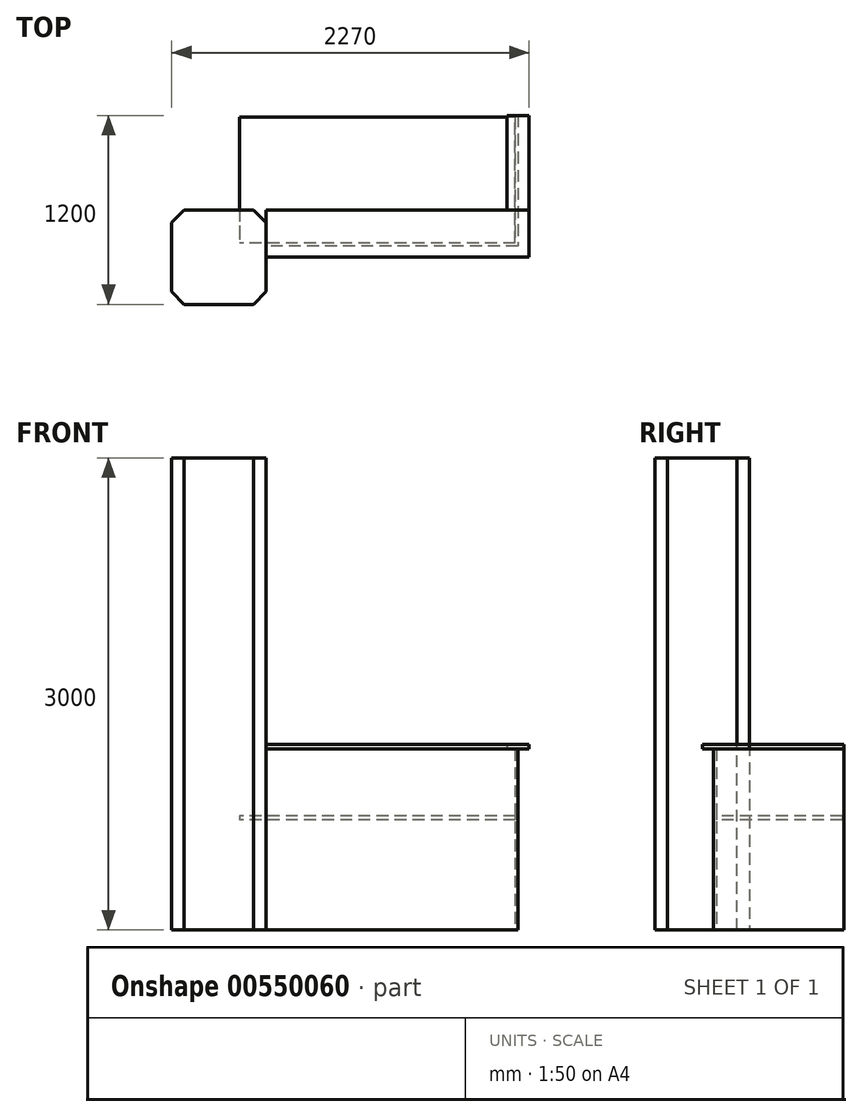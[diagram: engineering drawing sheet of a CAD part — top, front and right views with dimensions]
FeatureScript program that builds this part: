
annotation { "Feature Type Name" : "Feature", "Feature Type Description" : "" }
export const myFeature = defineFeature(function(context is Context, id is Id, definition is map)
    precondition{}
    {
        {
            var Q0;
            Q0=qCreatedBy(makeId("Top.planeOp"),FACE);
            var sketch = newSketch(context, id + "F0", { "sketchPlane" : qUnion([Q0])});
            skLineSegment(sketch, "E0.bottom", {"start": v(800, 9.5) * mm, "end": v(-800, 9.5) * mm});
            skLineSegment(sketch, "E0.top", {"start": v(800, -9.5) * mm, "end": v(-800, -9.5) * mm});
            skLineSegment(sketch, "E0.left", {"start": v(800, 9.5) * mm, "end": v(800, -9.5) * mm});
            skLineSegment(sketch, "E0.right", {"start": v(-800, 9.5) * mm, "end": v(-800, -9.5) * mm});
            skPoint(sketch, "E0.middle", {"position": v(0, 0) * mm});
            skLineSegment(sketch, "E1.bottom", {"start": v(800, 9.5) * mm, "end": v(781, 9.5) * mm});
            skLineSegment(sketch, "E1.top", {"start": v(800, 819.5) * mm, "end": v(781, 819.5) * mm});
            skLineSegment(sketch, "E1.left", {"start": v(800, 9.5) * mm, "end": v(800, 819.5) * mm});
            skLineSegment(sketch, "E1.right", {"start": v(781, 9.5) * mm, "end": v(781, 819.5) * mm});
            skSolve(sketch);
        }
        {
            var Q0;
            Q0 = qSketchRegion(id + "F0", true);
            extrude(context, id + "F1", {"entities" : qUnion([Q0]), "depth" : 1150 * mm, "offsetDistance" : 25 * mm});
        }
        {
            var Q0;
            Q0=qCreatedBy(makeId("Top.planeOp"),FACE);
            cPlane(context, id + "F2", {"entities" : qUnion([Q0]), "cplaneType" : CPlaneType.OFFSET, "offset" : 700 * mm, "width" : 150 * mm, "height" : 150 * mm});
        }
        {
            var Q0;
            Q0=qCreatedBy(id+"F2.planeOp",FACE);
            var sketch = newSketch(context, id + "F3", { "sketchPlane" : qUnion([Q0])});
            skLineSegment(sketch, "E2.bottom", {"start": v(781, 809.5) * mm, "end": v(-969, 809.5) * mm});
            skLineSegment(sketch, "E2.top", {"start": v(781, 9.5) * mm, "end": v(-969, 9.5) * mm});
            skLineSegment(sketch, "E2.left", {"start": v(781, 809.5) * mm, "end": v(781, 9.5) * mm});
            skLineSegment(sketch, "E2.right", {"start": v(-969, 809.5) * mm, "end": v(-969, 9.5) * mm});
            skSolve(sketch);
        }
        {
            var Q0;
            Q0=makeQuery(id+"F3.imprint","IMPRINT",FACE,{"disambiguationData":[TD([[makeQuery(id+"F3.imprint","IMPRINT",EDGE,{"derivedFrom":sQuery(id+"F3.wireOp",EDGE,"E2.bottom")}),1.0]])]});
            extrude(context, id + "F4", {"entities" : qUnion([Q0]), "depth" : 25 * mm, "offsetDistance" : 25 * mm});
        }
        {
            var Q0;
            Q0=qCreatedBy(makeId("Top.planeOp"),FACE);
            cPlane(context, id + "F5", {"entities" : qUnion([Q0]), "cplaneType" : CPlaneType.OFFSET, "offset" : 1150 * mm, "width" : 150 * mm, "height" : 150 * mm});
        }
        {
            var Q0;
            Q0=qCreatedBy(id+"F5.planeOp",FACE);
            var sketch = newSketch(context, id + "F6", { "sketchPlane" : qUnion([Q0])});
            skLineSegment(sketch, "E3.bottom", {"start": v(870, -79.5) * mm, "end": v(-800, -79.5) * mm});
            skLineSegment(sketch, "E3.top", {"start": v(870, 220.5) * mm, "end": v(-800, 220.5) * mm});
            skLineSegment(sketch, "E3.left", {"start": v(870, -79.5) * mm, "end": v(870, 220.5) * mm});
            skLineSegment(sketch, "E3.right", {"start": v(-800, -79.5) * mm, "end": v(-800, 220.5) * mm});
            skSolve(sketch);
        }
        {
            var Q0;
            Q0=makeQuery(id+"F6.imprint","IMPRINT",FACE,{"disambiguationData":[TD([[makeQuery(id+"F6.imprint","IMPRINT",EDGE,{"derivedFrom":sQuery(id+"F6.wireOp",EDGE,"E3.bottom")}),-1.0]])]});
            extrude(context, id + "F7", {"entities" : qUnion([Q0]), "depth" : 30 * mm, "offsetDistance" : 25 * mm});
        }
        {
            var Q0;
            Q0=qCreatedBy(id+"F5.planeOp",FACE);
            var sketch = newSketch(context, id + "F8", { "sketchPlane" : qUnion([Q0])});
            skLineSegment(sketch, "E4.bottom", {"start": v(870, 220.5) * mm, "end": v(730, 220.5) * mm});
            skLineSegment(sketch, "E4.top", {"start": v(870, 820.5) * mm, "end": v(730, 820.5) * mm});
            skLineSegment(sketch, "E4.left", {"start": v(870, 220.5) * mm, "end": v(870, 820.5) * mm});
            skLineSegment(sketch, "E4.right", {"start": v(730, 220.5) * mm, "end": v(730, 820.5) * mm});
            skSolve(sketch);
        }
        {
            var Q0;
            Q0 = qSketchRegion(id + "F8", true);
            extrude(context, id + "F9", {"entities" : qUnion([Q0]), "depth" : 30 * mm, "offsetDistance" : 25 * mm});
        }
        {
            var Q0;
            Q0=qCreatedBy(makeId("Top.planeOp"),FACE);
            var sketch = newSketch(context, id + "F10", { "sketchPlane" : qUnion([Q0])});
            skLineSegment(sketch, "E5.bottom", {"start": v(-800, -379.5) * mm, "end": v(-1400, -379.5) * mm});
            skLineSegment(sketch, "E5.top", {"start": v(-800, 220.5) * mm, "end": v(-1400, 220.5) * mm});
            skLineSegment(sketch, "E5.left", {"start": v(-800, -379.5) * mm, "end": v(-800, 220.5) * mm});
            skLineSegment(sketch, "E5.right", {"start": v(-1400, -379.5) * mm, "end": v(-1400, 220.5) * mm});
            skSolve(sketch);
        }
        {
            var Q0;
            Q0 = qSketchRegion(id + "F10", true);
            extrude(context, id + "F11", {"entities" : qUnion([Q0]), "depth" : 3000 * mm, "offsetDistance" : 25 * mm});
        }
        {
            var Q0;
            Q0=makeQuery(id+"F11.opExtrude","SWEPT_EDGE",EDGE,{"disambiguationData":[OSD([sQuery(id+"F10.wireOp",EDGE,"E5.top"),sQuery(id+"F10.wireOp",EDGE,"E5.left")])]});
            var Q1;
            Q1=makeQuery(id+"F11.opExtrude","SWEPT_EDGE",EDGE,{"disambiguationData":[OSD([sQuery(id+"F10.wireOp",EDGE,"E5.bottom"),sQuery(id+"F10.wireOp",EDGE,"E5.left")])]});
            var Q2;
            Q2=makeQuery(id+"F11.opExtrude","SWEPT_EDGE",EDGE,{"disambiguationData":[OSD([sQuery(id+"F10.wireOp",EDGE,"E5.top"),sQuery(id+"F10.wireOp",EDGE,"E5.right")])]});
            var Q3;
            Q3=makeQuery(id+"F11.opExtrude","SWEPT_EDGE",EDGE,{"disambiguationData":[OSD([sQuery(id+"F10.wireOp",EDGE,"E5.bottom"),sQuery(id+"F10.wireOp",EDGE,"E5.right")])]});
            chamfer(context, id + "F12", {"entities" : qUnion([Q0, Q1, Q2, Q3]), "width" : 80 * mm, "tangentPropagation" : true});
        }
    });
